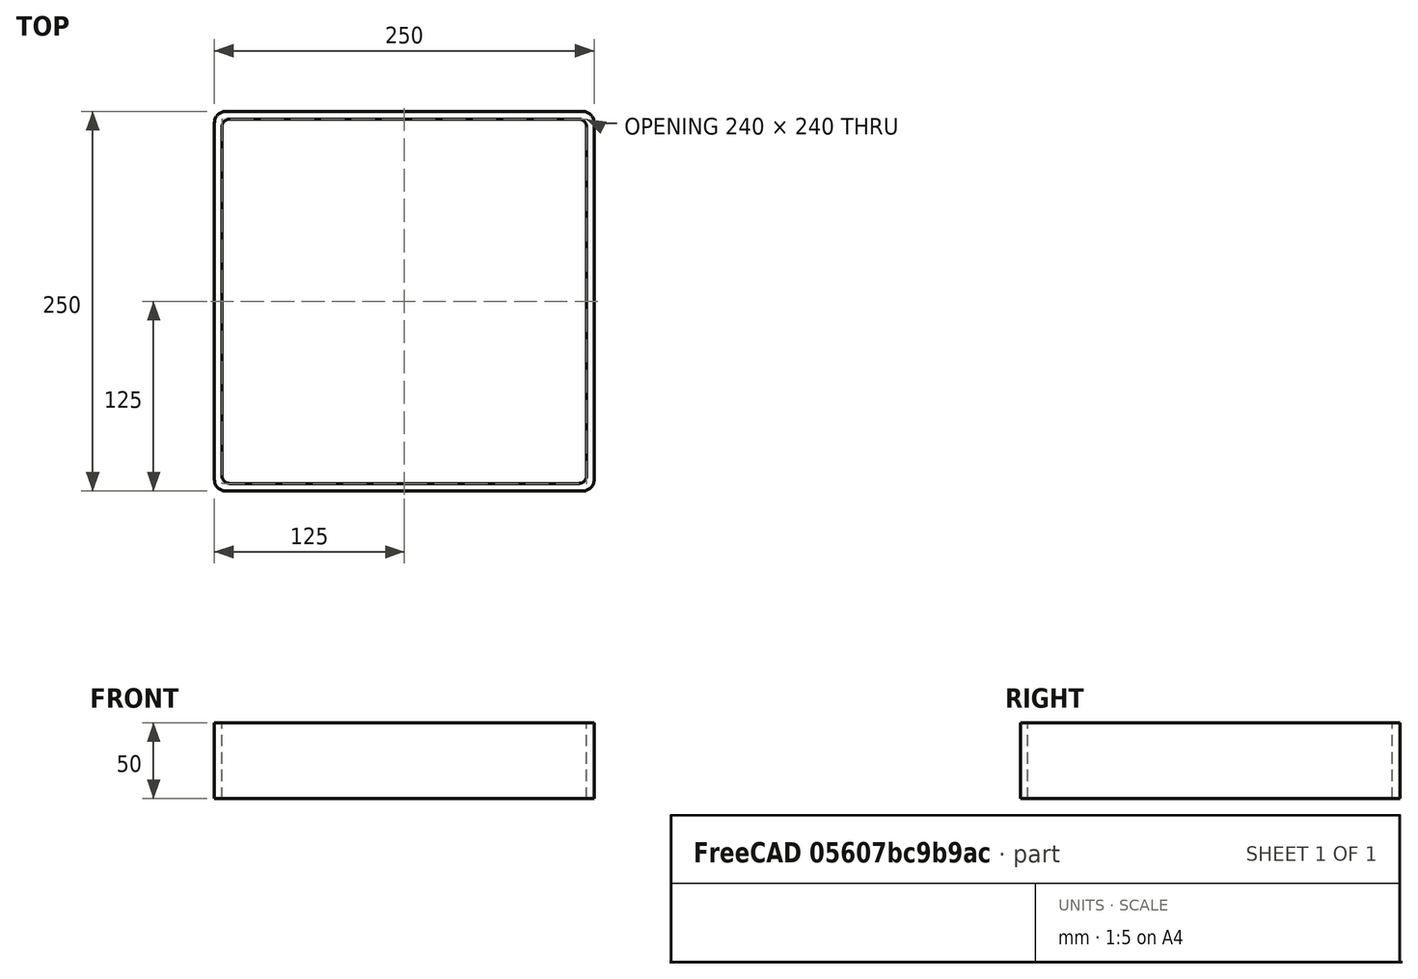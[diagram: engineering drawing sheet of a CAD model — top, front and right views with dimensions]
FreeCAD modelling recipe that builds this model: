
FCSTD DOCUMENT  (FreeCAD 0.15R4671 (Git))
Label: Square hollow section 250x250x5 EN10219 S235JRH
License: All rights reserved
LicenseURL: http://en.wikipedia.org/wiki/All_rights_reserved
objects: Sketcher::SketchObject×1, Part::Extrusion×1
note: 2 computed .brp shape members not serialized (recipe doc carries the construction recipe); baked Part::Feature solids carry a one-line shape summary decoded from their .brp

FEATURE [Sketcher::SketchObject] Sketch
  sketch-geometry (16):
    g0: LineSegment StartX=-115 StartY=120 StartZ=0 EndX=115 EndY=120 EndZ=0
    g1: LineSegment StartX=120 StartY=115 StartZ=0 EndX=120 EndY=-115 EndZ=0
    g2: LineSegment StartX=115 StartY=-120 StartZ=0 EndX=-115 EndY=-120 EndZ=0
    g3: LineSegment StartX=-120 StartY=-115 StartZ=0 EndX=-120 EndY=115 EndZ=0
    g4: LineSegment StartX=-117.5 StartY=125 StartZ=0 EndX=117.5 EndY=125 EndZ=0
    g5: LineSegment StartX=125 StartY=117.5 StartZ=0 EndX=125 EndY=-117.5 EndZ=0
    g6: LineSegment StartX=117.5 StartY=-125 StartZ=0 EndX=-117.5 EndY=-125 EndZ=0
    g7: LineSegment StartX=-125 StartY=-117.5 StartZ=0 EndX=-125 EndY=117.5 EndZ=0
    g8: ArcOfCircle CenterX=-115 CenterY=115 CenterZ=0 NormalX=0 NormalY=0 NormalZ=1 Radius=5 StartAngle=1.5708 EndAngle=3.14159
    g9: ArcOfCircle CenterX=115 CenterY=115 CenterZ=0 NormalX=0 NormalY=0 NormalZ=1 Radius=5 StartAngle=0 EndAngle=1.5708
    g10: ArcOfCircle CenterX=115 CenterY=-115 CenterZ=0 NormalX=0 NormalY=0 NormalZ=1 Radius=5 StartAngle=4.71239 EndAngle=6.28319
    g11: ArcOfCircle CenterX=-115 CenterY=-115 CenterZ=0 NormalX=0 NormalY=0 NormalZ=1 Radius=5 StartAngle=3.14159 EndAngle=4.71239
    g12: ArcOfCircle CenterX=117.5 CenterY=117.5 CenterZ=0 NormalX=0 NormalY=0 NormalZ=1 Radius=7.5 StartAngle=0 EndAngle=1.5708
    g13: ArcOfCircle CenterX=117.5 CenterY=-117.5 CenterZ=0 NormalX=0 NormalY=0 NormalZ=1 Radius=7.5 StartAngle=4.71239 EndAngle=6.28319
    g14: ArcOfCircle CenterX=-117.5 CenterY=-117.5 CenterZ=0 NormalX=0 NormalY=0 NormalZ=1 Radius=7.5 StartAngle=3.14159 EndAngle=4.71239
    g15: ArcOfCircle CenterX=-117.5 CenterY=117.5 CenterZ=0 NormalX=0 NormalY=0 NormalZ=1 Radius=7.5 StartAngle=1.5708 EndAngle=3.14159
  constraints (36):
    c: Horizontal(g2)
    c: Vertical(g3)
    c: Horizontal(g6)
    c: Vertical(g7)
    c: Tangent(g3,g8) = 1.5708
    c: Tangent(g0,g8) = 1.5708
    c: Tangent(g0,g9) = 1.5708
    c: Tangent(g1,g9) = 1.5708
    c: Tangent(g1,g10) = 1.5708
    c: Tangent(g2,g10) = 1.5708
    c: Tangent(g2,g11) = 1.5708
    c: Tangent(g3,g11) = 1.5708
    c: Tangent(g4,g12) = 1.5708
    c: Tangent(g5,g12) = 1.5708
    c: Tangent(g5,g13) = 1.5708
    c: Tangent(g6,g13) = 1.5708
    c: Tangent(g6,g14) = 1.5708
    c: Tangent(g7,g14) = 1.5708
    c: Tangent(g7,g15) = 1.5708
    c: Tangent(g4,g15) = 1.5708
    c: Equal(g9,g8)
    c: Equal(g9,g11)
    c: Equal(g9,g10)
    c: Equal(g12,g15)
    c: Equal(g12,g14)
    c: Equal(g12,g13)
    c: Symmetric(g4,g6,g-1)
    c: Symmetric(g7,g5,g-2)
    c: DistanceY(g4,g6) = -250
    c: DistanceX(g7,g5) = 250
    c: Symmetric(g3,g1,g-2)
    c: Symmetric(g0,g2,g-1)
    c: DistanceY(g0,g4) = 5
    c: DistanceX(g5,g1) = -5
    c: Radius(g9) = 5
    c: Radius(g12) = 7.5
FEATURE [Part::Extrusion] Extrude  label="Square hollow section 250x250x5 EN10219 S235JRH"
  Base = -> Sketch
  Dir = (0,0,50)
  Solid = true
